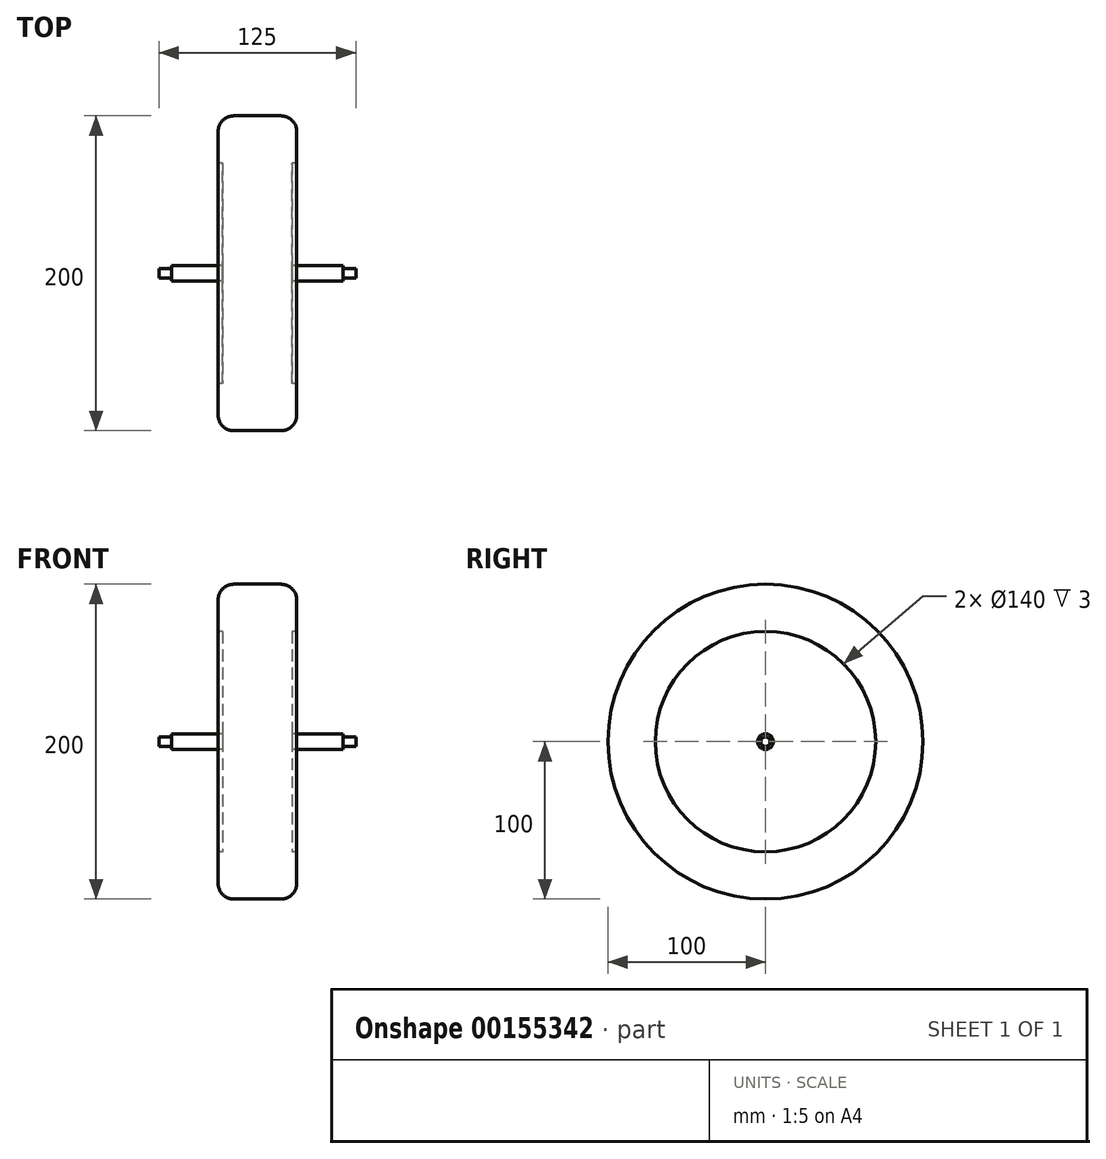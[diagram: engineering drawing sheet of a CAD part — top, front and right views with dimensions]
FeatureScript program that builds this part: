
annotation { "Feature Type Name" : "Feature", "Feature Type Description" : "" }
export const myFeature = defineFeature(function(context is Context, id is Id, definition is map)
    precondition{}
    {
        {
            var Q0;
            Q0=qCreatedBy(makeId("Front.planeOp"),FACE);
            var sketch = newSketch(context, id + "F0", { "sketchPlane" : qUnion([Q0])});
            skLineSegment(sketch, "E0", {"start": v(0, 70) * mm, "end": v(0, 90) * mm});
            skLineSegment(sketch, "E1", {"start": v(10, 100) * mm, "end": v(40, 100) * mm});
            skLineSegment(sketch, "E2", {"start": v(3, 70) * mm, "end": v(0, 70) * mm});
            skLineSegment(sketch, "E3", {"start": v(3, 70) * mm, "end": v(3, 4.98) * mm});
            skLineSegment(sketch, "E4", {"start": v(3, 0) * mm, "end": v(47, 0) * mm});
            skLineSegment(sketch, "E5", {"start": v(50, 90) * mm, "end": v(50, 70) * mm});
            skLineSegment(sketch, "E6", {"start": v(50, 70) * mm, "end": v(47, 70) * mm});
            skLineSegment(sketch, "E7", {"start": v(47, 70) * mm, "end": v(47, 4.98) * mm});
            skPoint(sketch, "E8.visualSharp", {"position": v(0, 100) * mm});
            skArc(sketch, "E8.filletArc", {"start": v(10, 100) * mm, "mid": v(2.93, 97.07) * mm, "end": v(0, 90) * mm});
            skPoint(sketch, "E9.visualSharp", {"position": v(50, 100) * mm});
            skArc(sketch, "E9.filletArc", {"start": v(50, 90) * mm, "mid": v(47.07, 97.07) * mm, "end": v(40, 100) * mm});
            skLineSegment(sketch, "E10", {"start": v(-61.98, 0) * mm, "end": v(-34.6, 0) * mm, "construction": true});
            skLineSegment(sketch, "E11.top", {"start": v(-37.5, 0) * mm, "end": v(87.5, 0) * mm});
            skLineSegment(sketch, "E11.left", {"start": v(-37.5, 2.98) * mm, "end": v(-37.5, 0) * mm});
            skLineSegment(sketch, "E12.left", {"start": v(-29.5, 4.98) * mm, "end": v(-29.5, 2.98) * mm});
            skLineSegment(sketch, "E13", {"start": v(-29.5, 2.98) * mm, "end": v(-37.5, 2.98) * mm});
            skPoint(sketch, "E14.orphan", {"position": v(-37.5, 4.98) * mm});
            skLineSegment(sketch, "E15", {"start": v(25, 100) * mm, "end": v(25, 0) * mm, "construction": true});
            skLineSegment(sketch, "E16.MirrorCS", {"start": v(79.5, 4.98) * mm, "end": v(79.5, 2.98) * mm});
            skLineSegment(sketch, "E17.MirrorCS", {"start": v(79.5, 2.98) * mm, "end": v(87.5, 2.98) * mm});
            skLineSegment(sketch, "E18.MirrorCS", {"start": v(87.5, 2.98) * mm, "end": v(87.5, 0) * mm});
            skPoint(sketch, "E19.MirrorP", {"position": v(87.5, 4.98) * mm});
            skLineSegment(sketch, "E20", {"start": v(25, 0) * mm, "end": v(25, -31.82) * mm});
            skLineSegment(sketch, "E21", {"start": v(-29.5, 4.98) * mm, "end": v(3, 4.98) * mm});
            skLineSegment(sketch, "E22.trimOffspring", {"start": v(47, 4.98) * mm, "end": v(79.5, 4.98) * mm});
            skSolve(sketch);
        }
        {
            var Q0;
            Q0=makeQuery(id+"F0.imprint","IMPRINT",FACE,{"disambiguationData":[TD([[makeQuery(id+"F0.imprint","IMPRINT",EDGE,{"derivedFrom":sQuery(id+"F0.wireOp",EDGE,"E0")}),-1.0]])]});
            var Q1;
            Q1=sQuery(id+"F0.wireOp",EDGE,"E10");
            revolve(context, id + "F1", {"entities" : qUnion([Q0]), "axis" : qUnion([Q1]), "revolveType" : RevolveType.FULL});
        }
    });
